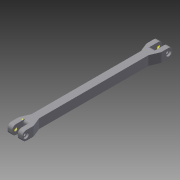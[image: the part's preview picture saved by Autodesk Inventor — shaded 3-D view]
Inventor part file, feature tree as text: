
AUTODESK INVENTOR PART (.ipt)
format: ipt  version: 2015 (Build 190159000, 159)  size: 172,544 bytes
history: native  units: mm
features: sketch x5, fillet x4, extrude x2, plane x2, mirror x2, loft x1, hole x1, other x1
ambient origin geometry x8: Origin, YZ Plane, XZ Plane, XY Plane, X Axis, Y Axis, Z Axis, Center Point
bodies: Solid1 (feature_tree)
feature tree (18):
  extrude  "Extrusion1"  Depth=10.0mm
  sketch  "Sketch2"  dims[d2=138.0mm d3=0.0mm d4=5.0mm]
  sketch  "Sketch3"  dims[d5=5.0mm d6=3.05mm d7=3.05mm d8=10.0mm]
  extrude  "Extrusion3"  Depth=5.0mm
  loft  "Loft2"
  plane  "Work Plane2"
  fillet  "Fillet4"  Radius=3.05mm
  fillet  "Fillet5"  Radius=10.0mm
  hole  "Hole1"  [1 undecoded]
  mirror  "Mirror2"
  plane  "Work Plane3"
  mirror  "Mirror3"
  fillet  "Fillet6"  [1 undecoded]
  fillet  "Fillet7"  Radius=4.0mm
  sketch  "Sketch8"  dims[d25=4.0mm d26=3.3mm d27=6.0mm d28=6.0mm d29=2.0mm d30=90.0deg d31=8.0mm d32=20.594885mm d42=3.0mm d43=3.0mm]
  sketch  "Sketch1"  dims[d0=8.0mm d1=10.0mm]
  other  "Edges1"
  sketch  "Sketch5"  dims[d18=12.0mm d19=0.0mm d20=0.0mm d21=90.0deg d22=0.0mm d23=90.0deg d24=4.0mm]
note: 2 required parameter values undecoded (feature->parameter linkage not recoverable at this tier; creation-order binding heuristic only, values carry confidence <= 0.55)
